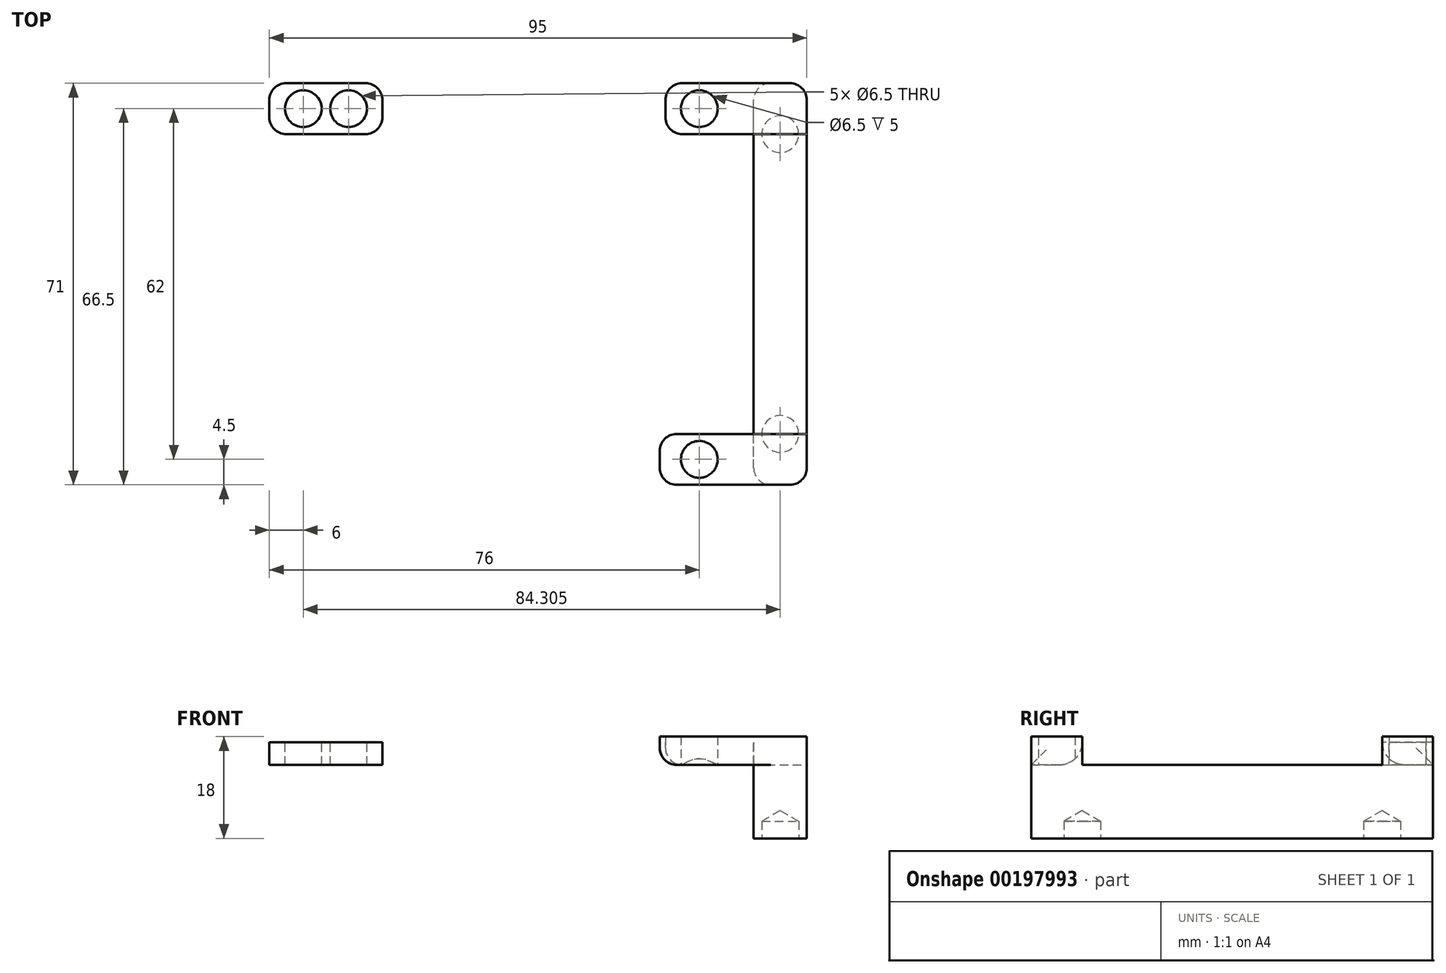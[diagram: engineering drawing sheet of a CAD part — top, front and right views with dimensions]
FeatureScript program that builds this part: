
annotation { "Feature Type Name" : "Feature", "Feature Type Description" : "" }
export const myFeature = defineFeature(function(context is Context, id is Id, definition is map)
    precondition{}
    {
        {
            var Q0;
            Q0=qCreatedBy(makeId("Top.planeOp"),FACE);
            var sketch = newSketch(context, id + "F0", { "sketchPlane" : qUnion([Q0])});
            skLineSegment(sketch, "E0.bottom", {"start": v(0, -35) * mm, "end": v(70, -35) * mm, "construction": true});
            skLineSegment(sketch, "E0.top", {"start": v(0, 35) * mm, "end": v(70, 35) * mm, "construction": true});
            skLineSegment(sketch, "E0.left", {"start": v(0, -35) * mm, "end": v(0, 35) * mm, "construction": true});
            skLineSegment(sketch, "E0.right", {"start": v(70, -35) * mm, "end": v(70, 35) * mm, "construction": true});
            skPoint(sketch, "E1", {"position": v(0, 0) * mm});
            skLineSegment(sketch, "E2.bottom", {"start": v(4, 31) * mm, "end": v(66, 31) * mm, "construction": true});
            skLineSegment(sketch, "E2.top", {"start": v(4, -31) * mm, "end": v(66, -31) * mm, "construction": true});
            skLineSegment(sketch, "E2.left", {"start": v(4, 31) * mm, "end": v(4, -31) * mm, "construction": true});
            skLineSegment(sketch, "E2.right", {"start": v(66, 31) * mm, "end": v(66, -31) * mm, "construction": true});
            skPoint(sketch, "E3", {"position": v(4, 0) * mm});
            skLineSegment(sketch, "E4", {"start": v(4, 31) * mm, "end": v(66, -31) * mm, "construction": true});
            skLineSegment(sketch, "E5", {"start": v(0, 35) * mm, "end": v(70, -35) * mm, "construction": true});
            skPoint(sketch, "E6", {"position": v(35, 0) * mm});
            skCircle(sketch, "E7", {"center": v(4, 31) * mm, "radius": 3.25 * mm, "construction": true});
            skCircle(sketch, "E8", {"center": v(66, 31) * mm, "radius": 3.25 * mm, "construction": true});
            skCircle(sketch, "E9.MirrorC", {"center": v(4, -31) * mm, "radius": 3.25 * mm, "construction": true});
            skCircle(sketch, "E10.MirrorC", {"center": v(66, -31) * mm, "radius": 3.25 * mm, "construction": true});
            skLineSegment(sketch, "E11.MirrorCS", {"start": v(-4, 31) * mm, "end": v(-66, -31) * mm, "construction": true});
            skPoint(sketch, "E12.MirrorP", {"position": v(-35, 0) * mm});
            skLineSegment(sketch, "E13.MirrorCS", {"start": v(0, 35) * mm, "end": v(-70, -35) * mm, "construction": true});
            skLineSegment(sketch, "E14.MirrorCS", {"start": v(-4, 31) * mm, "end": v(-66, 31) * mm, "construction": true});
            skLineSegment(sketch, "E15.MirrorCS", {"start": v(-70, -35) * mm, "end": v(-70, 35) * mm, "construction": true});
            skCircle(sketch, "E16.MirrorC", {"center": v(-66, 31) * mm, "radius": 3.25 * mm, "construction": true});
            skLineSegment(sketch, "E17.MirrorCS", {"start": v(-4, -31) * mm, "end": v(-66, -31) * mm, "construction": true});
            skLineSegment(sketch, "E18.MirrorCS", {"start": v(-4, 31) * mm, "end": v(-4, -31) * mm, "construction": true});
            skCircle(sketch, "E19.MirrorC", {"center": v(-4, 31) * mm, "radius": 3.25 * mm, "construction": true});
            skLineSegment(sketch, "E20.MirrorCS", {"start": v(-66, 31) * mm, "end": v(-66, -31) * mm, "construction": true});
            skLineSegment(sketch, "E21.MirrorCS", {"start": v(0, -35) * mm, "end": v(-70, -35) * mm, "construction": true});
            skLineSegment(sketch, "E22.MirrorCS", {"start": v(0, 35) * mm, "end": v(-70, 35) * mm, "construction": true});
            skCircle(sketch, "E23.MirrorC", {"center": v(-4, -31) * mm, "radius": 3.25 * mm, "construction": true});
            skPoint(sketch, "E24.MirrorP", {"position": v(-4, 0) * mm});
            skCircle(sketch, "E25.MirrorC", {"center": v(-66, -31) * mm, "radius": 3.25 * mm, "construction": true});
            skCircle(sketch, "E26", {"center": v(-35, 0) * mm, "radius": 34 * mm, "construction": true});
            skCircle(sketch, "E27.MirrorC", {"center": v(35, 0) * mm, "radius": 34 * mm, "construction": true});
            skLineSegment(sketch, "E28.bottom", {"start": v(10, 26.5) * mm, "end": v(-10, 26.5) * mm});
            skLineSegment(sketch, "E28.top", {"start": v(10, 35.5) * mm, "end": v(-10, 35.5) * mm});
            skLineSegment(sketch, "E28.left", {"start": v(10, 26.5) * mm, "end": v(10, 35.5) * mm});
            skLineSegment(sketch, "E28.right", {"start": v(-10, 26.5) * mm, "end": v(-10, 35.5) * mm});
            skPoint(sketch, "E28.middle", {"position": v(0, 31) * mm});
            skSolve(sketch);
        }
        {
            var Q0;
            Q0=makeQuery(id+"F0.imprint","IMPRINT",FACE,{"disambiguationData":[TD([[makeQuery(id+"F0.imprint","IMPRINT",EDGE,{"derivedFrom":sQuery(id+"F0.wireOp",EDGE,"E28.bottom")}),-1.0]])]});
            extrude(context, id + "F1", {"entities" : qUnion([Q0]), "depth" : 4 * mm});
        }
        {
            var Q0;
            Q0=makeQuery(id+"F1.opExtrude","CAP_FACE",FACE,{"disambiguationData":[OSD([sQuery(id+"F0.wireOp",EDGE,"E28.bottom"),sQuery(id+"F0.wireOp",EDGE,"E28.top"),sQuery(id+"F0.wireOp",EDGE,"E28.left"),sQuery(id+"F0.wireOp",EDGE,"E28.right")])],"isStart":false});
            var sketch = newSketch(context, id + "F2", { "sketchPlane" : qUnion([Q0])});
            skCircle(sketch, "E29", {"center": v(-4, 31) * mm, "radius": 3.35 * mm});
            skCircle(sketch, "E30", {"center": v(4, 31) * mm, "radius": 3.35 * mm});
            skSolve(sketch);
        }
        {
            var Q0;
            Q0=sQuery(id+"F2.wireOp",VERTEX,"E29.center");
            var Q1;
            Q1=sQuery(id+"F2.wireOp",VERTEX,"E30.center");
            var Q2;
            Q2=makeQuery(id+"F1.opExtrude","SWEPT_BODY",BODY,{"disambiguationData":[OSD([sQuery(id+"F0.wireOp",EDGE,"E28.bottom"),sQuery(id+"F0.wireOp",EDGE,"E28.top"),sQuery(id+"F0.wireOp",EDGE,"E28.left"),sQuery(id+"F0.wireOp",EDGE,"E28.right")])]});
            hole(context, id + "F3", {"style" : HoleStyle.SIMPLE, "endStyle" : HoleEndStyle.THROUGH, "holeDiameter" : 6.5 * mm, "locations" : qUnion([Q0, Q1]), "scope" : qUnion([Q2]), "isTappedThrough" : true});
        }
        {
            var Q0;
            Q0=makeQuery(id+"F1.opExtrude","SWEPT_EDGE",EDGE,{"disambiguationData":[OSD([sQuery(id+"F0.wireOp",EDGE,"E28.top"),sQuery(id+"F0.wireOp",EDGE,"E28.left")])]});
            var Q1;
            Q1=makeQuery(id+"F1.opExtrude","SWEPT_EDGE",EDGE,{"disambiguationData":[OSD([sQuery(id+"F0.wireOp",EDGE,"E28.bottom"),sQuery(id+"F0.wireOp",EDGE,"E28.left")])]});
            var Q2;
            Q2=makeQuery(id+"F1.opExtrude","SWEPT_EDGE",EDGE,{"disambiguationData":[OSD([sQuery(id+"F0.wireOp",EDGE,"E28.bottom"),sQuery(id+"F0.wireOp",EDGE,"E28.right")])]});
            var Q3;
            Q3=makeQuery(id+"F1.opExtrude","SWEPT_EDGE",EDGE,{"disambiguationData":[OSD([sQuery(id+"F0.wireOp",EDGE,"E28.top"),sQuery(id+"F0.wireOp",EDGE,"E28.right")])]});
            fillet(context, id + "F4", {"entities" : qUnion([Q0, Q1, Q2, Q3]), "radius" : 3 * mm, "tangentPropagation" : true, "allowEdgeOverflow" : false});
        }
        {
            var Q0;
            Q0=qCreatedBy(makeId("Top.planeOp"),FACE);
            var sketch = newSketch(context, id + "F5", { "sketchPlane" : qUnion([Q0])});
            skLineSegment(sketch, "E31.bottom", {"start": v(60, 26.5) * mm, "end": v(75.61, 26.5) * mm});
            skLineSegment(sketch, "E31.top", {"start": v(60, 35.5) * mm, "end": v(85, 35.5) * mm});
            skLineSegment(sketch, "E31.left", {"start": v(60, 26.5) * mm, "end": v(60, 35.5) * mm});
            skLineSegment(sketch, "E31.right", {"start": v(85, 26.5) * mm, "end": v(85, 35.5) * mm});
            skLineSegment(sketch, "E32.bottom", {"start": v(75.61, 35.5) * mm, "end": v(85, 35.5) * mm});
            skLineSegment(sketch, "E32.top", {"start": v(75.61, -35.5) * mm, "end": v(85, -35.5) * mm});
            skLineSegment(sketch, "E32.right", {"start": v(85, 35.5) * mm, "end": v(85, 26.5) * mm});
            skLineSegment(sketch, "E33.bottom", {"start": v(85, -35.5) * mm, "end": v(59, -35.5) * mm});
            skLineSegment(sketch, "E33.top", {"start": v(75.61, -26.5) * mm, "end": v(59, -26.5) * mm});
            skLineSegment(sketch, "E33.left", {"start": v(85, -35.5) * mm, "end": v(85, -26.5) * mm});
            skLineSegment(sketch, "E33.right", {"start": v(59, -35.5) * mm, "end": v(59, -26.5) * mm});
            skLineSegment(sketch, "E34", {"start": v(75.61, -26.5) * mm, "end": v(85, -26.5) * mm});
            skLineSegment(sketch, "E35", {"start": v(75.61, 26.5) * mm, "end": v(85, 26.5) * mm});
            skLineSegment(sketch, "E36.trimOffspring", {"start": v(85, -26.5) * mm, "end": v(85, -35.5) * mm});
            skPoint(sketch, "E37", {"position": v(80.3, -26.5) * mm});
            skPoint(sketch, "E38", {"position": v(80.3, 26.5) * mm});
            skSolve(sketch);
        }
        {
            var Q0;
            Q0=makeQuery(id+"F5.imprint","IMPRINT",FACE,{"disambiguationData":[TD([[makeQuery(id+"F5.imprint","IMPRINT",EDGE,{"derivedFrom":sQuery(id+"F5.wireOp",EDGE,"E31.bottom")}),1.0]])]});
            var Q1;
            Q1=makeQuery(id+"F5.imprint","IMPRINT",FACE,{"disambiguationData":[TD([[makeQuery(id+"F5.imprint","IMPRINT",EDGE,{"derivedFrom":sQuery(id+"F5.wireOp",EDGE,"E33.top")}),1.0]])]});
            extrude(context, id + "F6", {"entities" : qUnion([Q0, Q1]), "depth" : 5 * mm});
        }
        {
            var Q0;
            Q0=makeQuery(id+"F6.opExtrude","CAP_FACE",FACE,{"disambiguationData":[OSD([sQuery(id+"F5.wireOp",EDGE,"E33.bottom"),sQuery(id+"F5.wireOp",EDGE,"E33.top"),sQuery(id+"F5.wireOp",EDGE,"E33.right"),sQuery(id+"F5.wireOp",EDGE,"E34"),sQuery(id+"F5.wireOp",EDGE,"E36.trimOffspring")])],"isStart":true});
            var sketch = newSketch(context, id + "F7", { "sketchPlane" : qUnion([Q0])});
            skLineSegment(sketch, "E39.bottom", {"start": v(75.61, 35.5) * mm, "end": v(85, 35.5) * mm});
            skLineSegment(sketch, "E39.top", {"start": v(75.61, -35.5) * mm, "end": v(85, -35.5) * mm});
            skLineSegment(sketch, "E39.left", {"start": v(75.61, 35.5) * mm, "end": v(75.61, -35.5) * mm});
            skLineSegment(sketch, "E39.right", {"start": v(85, 35.5) * mm, "end": v(85, -35.5) * mm});
            skSolve(sketch);
        }
        {
            var Q0;
            {var subQ0=sQuery(id+"F7.wireOp",EDGE,"E39.top");Q0=makeQuery(id+"F7.imprint","IMPRINT",FACE,{"disambiguationData":[TD([[makeQuery(id+"F7.imprint","IMPRINT",EDGE,{"derivedFrom":subQ0}),1.0]])]});}
            var Q1;
            {var subQ0=sQuery(id+"F7.wireOp",EDGE,"E39.bottom");Q1=makeQuery(id+"F7.imprint","IMPRINT",FACE,{"disambiguationData":[TD([[makeQuery(id+"F7.imprint","IMPRINT",EDGE,{"derivedFrom":subQ0}),1.0]])]});}
            extrude(context, id + "F8", {"entities" : qUnion([Q0, Q1]), "depth" : 13 * mm});
        }
        {
            var Q0;
            Q0=makeQuery(id+"F6.opExtrude","SWEPT_BODY",BODY,{"disambiguationData":[OSD([sQuery(id+"F5.wireOp",EDGE,"E31.bottom"),sQuery(id+"F5.wireOp",EDGE,"E31.top"),sQuery(id+"F5.wireOp",EDGE,"E31.left"),sQuery(id+"F5.wireOp",EDGE,"E32.bottom"),sQuery(id+"F5.wireOp",EDGE,"E32.right"),sQuery(id+"F5.wireOp",EDGE,"E35")])]});
            var Q1;
            Q1=makeQuery(id+"F6.opExtrude","SWEPT_BODY",BODY,{"disambiguationData":[OSD([sQuery(id+"F5.wireOp",EDGE,"E33.bottom"),sQuery(id+"F5.wireOp",EDGE,"E33.top"),sQuery(id+"F5.wireOp",EDGE,"E33.right"),sQuery(id+"F5.wireOp",EDGE,"E34"),sQuery(id+"F5.wireOp",EDGE,"E36.trimOffspring")])]});
            var Q2;
            Q2=makeQuery(id+"F8.opExtrude","SWEPT_BODY",BODY,{"disambiguationData":[OSD([sQuery(id+"F7.wireOp",EDGE,"E39.bottom"),sQuery(id+"F7.wireOp",EDGE,"E39.top"),sQuery(id+"F7.wireOp",EDGE,"E39.left"),sQuery(id+"F7.wireOp",EDGE,"E39.right")])]});
            booleanBodies(context, id + "F9", {"operationType" : BooleanOperationType.UNION, "tools" : qUnion([Q0, Q1, Q2])});
        }
        {
            var Q0;
            {var subQ0=sQuery(id+"F5.wireOp",EDGE,"E32.right");var subQ1=sQuery(id+"F5.wireOp",EDGE,"E35");var subQ2=sQuery(id+"F5.wireOp",EDGE,"E31.bottom");Q0=makeQuery(id+"F9.opBoolean","SPLIT",EDGE,{"disambiguationData":[TD([makeQuery(id+"F6.opExtrude","SWEPT_FACE",FACE,{"disambiguationData":[OSD([subQ0])]})])],"derivedFrom":makeQuery(id+"F6.opExtrude","CAP_EDGE",EDGE,{"disambiguationData":[OSD([subQ2,subQ1])],"isStart":true})});}
            var Q1;
            {var subQ0=sQuery(id+"F5.wireOp",EDGE,"E34");var subQ1=sQuery(id+"F5.wireOp",EDGE,"E33.top");Q1=makeQuery(id+"F9.opBoolean","SPLIT",EDGE,{"disambiguationData":[TD([makeQuery(id+"F6.opExtrude","SWEPT_FACE",FACE,{"disambiguationData":[OSD([sQuery(id+"F5.wireOp",EDGE,"E32.right")])]})])],"derivedFrom":makeQuery(id+"F6.opExtrude","CAP_EDGE",EDGE,{"disambiguationData":[OSD([subQ1,subQ0])],"isStart":true})});}
            fillet(context, id + "F10", {"entities" : qUnion([Q0, Q1]), "radius" : 4 * mm, "tangentPropagation" : true, "allowEdgeOverflow" : false});
        }
        {
            var Q0;
            Q0=makeQuery(id+"F6.opExtrude","SWEPT_EDGE",EDGE,{"disambiguationData":[OSD([sQuery(id+"F5.wireOp",EDGE,"E31.bottom"),sQuery(id+"F5.wireOp",EDGE,"E31.left")])]});
            var Q1;
            Q1=makeQuery(id+"F6.opExtrude","SWEPT_EDGE",EDGE,{"disambiguationData":[OSD([sQuery(id+"F5.wireOp",EDGE,"E31.top"),sQuery(id+"F5.wireOp",EDGE,"E31.left")])]});
            var Q2;
            Q2=makeQuery(id+"F9.opBoolean","MERGE",EDGE,{"derivedFrom":[makeQuery(id+"F6.opExtrude","SWEPT_EDGE",EDGE,{"disambiguationData":[OSD([sQuery(id+"F5.wireOp",EDGE,"E32.bottom"),sQuery(id+"F5.wireOp",EDGE,"E32.right")])]}),makeQuery(id+"F8.opExtrude","SWEPT_EDGE",EDGE,{"disambiguationData":[OSD([sQuery(id+"F7.wireOp",EDGE,"E39.top"),sQuery(id+"F7.wireOp",EDGE,"E39.right")])]})]});
            var Q3;
            Q3=makeQuery(id+"F9.opBoolean","MERGE",EDGE,{"derivedFrom":[makeQuery(id+"F6.opExtrude","SWEPT_EDGE",EDGE,{"disambiguationData":[OSD([sQuery(id+"F5.wireOp",EDGE,"E33.bottom"),sQuery(id+"F5.wireOp",EDGE,"E36.trimOffspring")])]}),makeQuery(id+"F8.opExtrude","SWEPT_EDGE",EDGE,{"disambiguationData":[OSD([sQuery(id+"F7.wireOp",EDGE,"E39.bottom"),sQuery(id+"F7.wireOp",EDGE,"E39.right")])]})]});
            var Q4;
            Q4=makeQuery(id+"F6.opExtrude","SWEPT_EDGE",EDGE,{"disambiguationData":[OSD([sQuery(id+"F5.wireOp",EDGE,"E33.bottom"),sQuery(id+"F5.wireOp",EDGE,"E33.right")])]});
            var Q5;
            Q5=makeQuery(id+"F6.opExtrude","SWEPT_EDGE",EDGE,{"disambiguationData":[OSD([sQuery(id+"F5.wireOp",EDGE,"E33.top"),sQuery(id+"F5.wireOp",EDGE,"E33.right")])]});
            var Q6;
            Q6=makeQuery(id+"F8.opExtrude","SWEPT_EDGE",EDGE,{"disambiguationData":[OSD([sQuery(id+"F7.wireOp",EDGE,"E39.top"),sQuery(id+"F7.wireOp",EDGE,"E39.left")])]});
            var Q7;
            Q7=makeQuery(id+"F8.opExtrude","SWEPT_EDGE",EDGE,{"disambiguationData":[OSD([sQuery(id+"F5.wireOp",EDGE,"E33.bottom"),sQuery(id+"F7.wireOp",EDGE,"E39.bottom"),sQuery(id+"F7.wireOp",EDGE,"E39.left")])]});
            fillet(context, id + "F11", {"entities" : qUnion([Q0, Q1, Q2, Q3, Q4, Q5, Q6, Q7]), "radius" : 3 * mm, "tangentPropagation" : true, "allowEdgeOverflow" : false});
        }
        {
            var Q0;
            Q0=sQuery(id+"F0.wireOp",VERTEX,"E8.center");
            var Q1;
            Q1=sQuery(id+"F0.wireOp",VERTEX,"E4.end");
            var Q2;
            Q2=makeQuery(id+"F6.opExtrude","SWEPT_BODY",BODY,{"disambiguationData":[OSD([sQuery(id+"F5.wireOp",EDGE,"E31.bottom"),sQuery(id+"F5.wireOp",EDGE,"E31.top"),sQuery(id+"F5.wireOp",EDGE,"E31.left"),sQuery(id+"F5.wireOp",EDGE,"E32.bottom"),sQuery(id+"F5.wireOp",EDGE,"E32.right"),sQuery(id+"F5.wireOp",EDGE,"E35")])]});
            hole(context, id + "F12", {"style" : HoleStyle.SIMPLE, "endStyle" : HoleEndStyle.THROUGH, "oppositeDirection" : true, "holeDiameter" : 6.5 * mm, "locations" : qUnion([Q0, Q1]), "scope" : qUnion([Q2]), "isTappedThrough" : true});
        }
        {
            var Q0;
            Q0=makeQuery(id+"F8.opExtrude","CAP_FACE",FACE,{"disambiguationData":[OSD([sQuery(id+"F7.wireOp",EDGE,"E39.bottom"),sQuery(id+"F7.wireOp",EDGE,"E39.top"),sQuery(id+"F7.wireOp",EDGE,"E39.left"),sQuery(id+"F7.wireOp",EDGE,"E39.right")])],"isStart":false});
            var sketch = newSketch(context, id + "F13", { "sketchPlane" : qUnion([Q0])});
            skPoint(sketch, "E40", {"position": v(80.3, 26.5) * mm});
            skPoint(sketch, "E41", {"position": v(80.3, -26.5) * mm});
            skSolve(sketch);
        }
        {
            var Q0;
            Q0=sQuery(id+"F13.wireOp",VERTEX,"E40");
            var Q1;
            Q1=sQuery(id+"F13.wireOp",VERTEX,"E41");
            var Q2;
            Q2=makeQuery(id+"F6.opExtrude","SWEPT_BODY",BODY,{"disambiguationData":[OSD([sQuery(id+"F5.wireOp",EDGE,"E31.bottom"),sQuery(id+"F5.wireOp",EDGE,"E31.top"),sQuery(id+"F5.wireOp",EDGE,"E31.left"),sQuery(id+"F5.wireOp",EDGE,"E32.bottom"),sQuery(id+"F5.wireOp",EDGE,"E32.right"),sQuery(id+"F5.wireOp",EDGE,"E35")])]});
            hole(context, id + "F14", {"style" : HoleStyle.SIMPLE, "endStyle" : HoleEndStyle.BLIND, "holeDiameter" : 6.5 * mm, "holeDepth" : 3 * mm, "locations" : qUnion([Q0, Q1]), "scope" : qUnion([Q2])});
        }
    });
